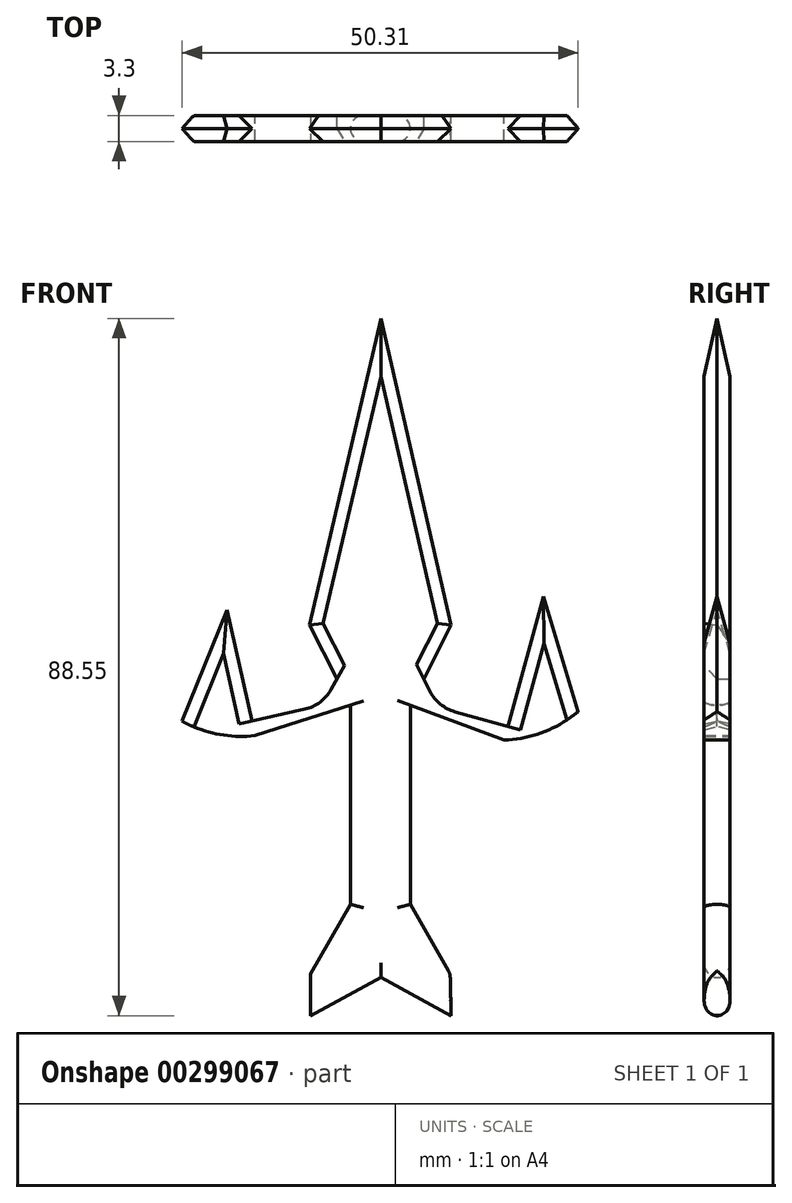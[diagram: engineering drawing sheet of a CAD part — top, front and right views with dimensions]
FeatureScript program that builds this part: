
annotation { "Feature Type Name" : "Feature", "Feature Type Description" : "" }
export const myFeature = defineFeature(function(context is Context, id is Id, definition is map)
    precondition{}
    {
        {
            var Q0;
            Q0=qCreatedBy(makeId("Front.planeOp"),FACE);
            var sketch = newSketch(context, id + "F0", { "sketchPlane" : qUnion([Q0])});
            skLineSegment(sketch, "E0", {"start": v(-8.93, -32.58) * mm, "end": v(0, -27.74) * mm});
            skLineSegment(sketch, "E1", {"start": v(0, -27.74) * mm, "end": v(8.93, -32.58) * mm});
            skLineSegment(sketch, "E2", {"start": v(-8.93, -32.58) * mm, "end": v(-8.93, -27.25) * mm});
            skLineSegment(sketch, "E3", {"start": v(-8.93, -27.25) * mm, "end": v(-3.88, -18.44) * mm});
            skLineSegment(sketch, "E4", {"start": v(-3.88, -18.44) * mm, "end": v(3.74, -18.44) * mm});
            skLineSegment(sketch, "E5", {"start": v(3.74, -18.44) * mm, "end": v(8.8, -27.25) * mm});
            skLineSegment(sketch, "E6", {"start": v(8.8, -27.25) * mm, "end": v(8.93, -32.58) * mm});
            skLineSegment(sketch, "E7", {"start": v(-3.88, -18.44) * mm, "end": v(-3.88, 6.85) * mm});
            skLineSegment(sketch, "E8", {"start": v(3.74, -18.44) * mm, "end": v(3.74, 6.85) * mm});
            skArc(sketch, "E9", {"start": v(-25.25, 4.84) * mm, "mid": v(-20.76, 3.19) * mm, "end": v(-15.98, 3) * mm});
            skArc(sketch, "E10", {"start": v(15.65, 2.42) * mm, "mid": v(20.67, 3.44) * mm, "end": v(25.06, 6.07) * mm});
            skLineSegment(sketch, "E11", {"start": v(-25.25, 4.84) * mm, "end": v(-19.55, 18.97) * mm});
            skLineSegment(sketch, "E12", {"start": v(-19.55, 18.97) * mm, "end": v(-15.98, 3) * mm});
            skLineSegment(sketch, "E13", {"start": v(25.06, 6.07) * mm, "end": v(20.67, 20.66) * mm});
            skPoint(sketch, "E13.endSnap0", {"position": v(20.67, 3.44) * mm});
            skLineSegment(sketch, "E14", {"start": v(20.67, 20.66) * mm, "end": v(15.65, 2.42) * mm});
            skLineSegment(sketch, "E15", {"start": v(-3.88, 6.85) * mm, "end": v(-9.07, 17.03) * mm});
            skLineSegment(sketch, "E16", {"start": v(3.74, 6.85) * mm, "end": v(8.94, 17.03) * mm});
            skLineSegment(sketch, "E17", {"start": v(-9.07, 17.03) * mm, "end": v(0, 55.97) * mm});
            skLineSegment(sketch, "E18", {"start": v(0, 55.97) * mm, "end": v(8.94, 17.03) * mm});
            skLineSegment(sketch, "E19", {"start": v(-5.58, 10.2) * mm, "end": v(-7.45, 6.85) * mm});
            skLineSegment(sketch, "E20", {"start": v(5.45, 10.2) * mm, "end": v(7.27, 6.62) * mm});
            skLineSegment(sketch, "E21", {"start": v(-7.45, 6.85) * mm, "end": v(-16.4, 4.85) * mm});
            skLineSegment(sketch, "E22", {"start": v(7.27, 6.62) * mm, "end": v(16.13, 4.18) * mm});
            skLineSegment(sketch, "E23", {"start": v(-15.98, 3) * mm, "end": v(-3.88, 6.85) * mm});
            skLineSegment(sketch, "E24", {"start": v(3.74, 6.85) * mm, "end": v(15.65, 2.42) * mm});
            skSolve(sketch);
        }
        {
            var Q0;
            Q0 = qSketchRegion(id + "F0", true);
            extrude(context, id + "F1", {"entities" : qUnion([Q0]), "depth" : 3.3 * mm});
        }
        {
            var Q0;
            Q0=makeQuery(id+"F1.opExtrude","CAP_EDGE",EDGE,{"disambiguationData":[OSD([sQuery(id+"F0.wireOp",EDGE,"E18")])],"isStart":false});
            var Q1;
            Q1=makeQuery(id+"F1.opExtrude","CAP_EDGE",EDGE,{"disambiguationData":[OSD([sQuery(id+"F0.wireOp",EDGE,"E17")])],"isStart":false});
            var Q2;
            Q2=makeQuery(id+"F1.opExtrude","CAP_EDGE",EDGE,{"disambiguationData":[OSD([sQuery(id+"F0.wireOp",EDGE,"E14")])],"isStart":false});
            var Q3;
            Q3=makeQuery(id+"F1.opExtrude","CAP_EDGE",EDGE,{"disambiguationData":[OSD([sQuery(id+"F0.wireOp",EDGE,"E13")])],"isStart":false});
            var Q4;
            Q4=makeQuery(id+"F1.opExtrude","CAP_EDGE",EDGE,{"disambiguationData":[OSD([sQuery(id+"F0.wireOp",EDGE,"E11")])],"isStart":false});
            var Q5;
            Q5=makeQuery(id+"F1.opExtrude","CAP_EDGE",EDGE,{"disambiguationData":[OSD([sQuery(id+"F0.wireOp",EDGE,"E12")])],"isStart":false});
            var Q6;
            Q6=makeQuery(id+"F1.opExtrude","CAP_EDGE",EDGE,{"disambiguationData":[OSD([sQuery(id+"F0.wireOp",EDGE,"E14")])],"isStart":true});
            var Q7;
            Q7=makeQuery(id+"F1.opExtrude","CAP_EDGE",EDGE,{"disambiguationData":[OSD([sQuery(id+"F0.wireOp",EDGE,"E13")])],"isStart":true});
            var Q8;
            Q8=makeQuery(id+"F1.opExtrude","CAP_EDGE",EDGE,{"disambiguationData":[OSD([sQuery(id+"F0.wireOp",EDGE,"E11")])],"isStart":true});
            var Q9;
            Q9=makeQuery(id+"F1.opExtrude","CAP_EDGE",EDGE,{"disambiguationData":[OSD([sQuery(id+"F0.wireOp",EDGE,"E12")])],"isStart":true});
            var Q10;
            Q10=makeQuery(id+"F1.opExtrude","CAP_EDGE",EDGE,{"disambiguationData":[OSD([sQuery(id+"F0.wireOp",EDGE,"E16")])],"isStart":false});
            var Q11;
            Q11=makeQuery(id+"F1.opExtrude","CAP_EDGE",EDGE,{"disambiguationData":[OSD([sQuery(id+"F0.wireOp",EDGE,"E15")])],"isStart":false});
            var Q12;
            Q12=makeQuery(id+"F1.opExtrude","CAP_EDGE",EDGE,{"disambiguationData":[OSD([sQuery(id+"F0.wireOp",EDGE,"E18")])],"isStart":true});
            var Q13;
            Q13=makeQuery(id+"F1.opExtrude","CAP_EDGE",EDGE,{"disambiguationData":[OSD([sQuery(id+"F0.wireOp",EDGE,"E17")])],"isStart":true});
            chamfer(context, id + "F2", {"entities" : qUnion([Q0, Q1, Q2, Q3, Q4, Q5, Q6, Q7, Q8, Q9, Q10, Q11, Q12, Q13]), "width" : 1.65 * mm, "tangentPropagation" : true});
        }
        {
            var Q0;
            Q0=makeQuery(id+"F1.opExtrude","SWEPT_EDGE",EDGE,{"disambiguationData":[OSD([sQuery(id+"F0.wireOp",EDGE,"E19"),sQuery(id+"F0.wireOp",EDGE,"E21")])]});
            var Q1;
            Q1=makeQuery(id+"F1.opExtrude","SWEPT_EDGE",EDGE,{"disambiguationData":[OSD([sQuery(id+"F0.wireOp",EDGE,"E20"),sQuery(id+"F0.wireOp",EDGE,"E22")])]});
            fillet(context, id + "F3", {"entities" : qUnion([Q0, Q1]), "radius" : 5.08 * mm, "tangentPropagation" : true, "allowEdgeOverflow" : false});
        }
        {
            var Q0;
            Q0=makeQuery(id+"F1.opExtrude","CAP_EDGE",EDGE,{"disambiguationData":[OSD([sQuery(id+"F0.wireOp",EDGE,"E7")])],"isStart":false});
            var Q1;
            Q1=makeQuery(id+"F1.opExtrude","CAP_EDGE",EDGE,{"disambiguationData":[OSD([sQuery(id+"F0.wireOp",EDGE,"E8")])],"isStart":false});
            var Q2;
            Q2=makeQuery(id+"F1.opExtrude","CAP_EDGE",EDGE,{"disambiguationData":[OSD([sQuery(id+"F0.wireOp",EDGE,"E7")])],"isStart":true});
            var Q3;
            Q3=makeQuery(id+"F1.opExtrude","CAP_EDGE",EDGE,{"disambiguationData":[OSD([sQuery(id+"F0.wireOp",EDGE,"E8")])],"isStart":true});
            var Q4;
            Q4=makeQuery(id+"F1.opExtrude","CAP_EDGE",EDGE,{"disambiguationData":[OSD([sQuery(id+"F0.wireOp",EDGE,"E3")])],"isStart":true});
            var Q5;
            Q5=makeQuery(id+"F1.opExtrude","CAP_EDGE",EDGE,{"disambiguationData":[OSD([sQuery(id+"F0.wireOp",EDGE,"E3")])],"isStart":false});
            var Q6;
            Q6=makeQuery(id+"F1.opExtrude","CAP_EDGE",EDGE,{"disambiguationData":[OSD([sQuery(id+"F0.wireOp",EDGE,"E0")])],"isStart":true});
            var Q7;
            Q7=makeQuery(id+"F1.opExtrude","CAP_EDGE",EDGE,{"disambiguationData":[OSD([sQuery(id+"F0.wireOp",EDGE,"E0")])],"isStart":false});
            var Q8;
            Q8=makeQuery(id+"F1.opExtrude","CAP_EDGE",EDGE,{"disambiguationData":[OSD([sQuery(id+"F0.wireOp",EDGE,"E5")])],"isStart":false});
            var Q9;
            Q9=makeQuery(id+"F1.opExtrude","SWEPT_EDGE",EDGE,{"disambiguationData":[OSD([sQuery(id+"F0.wireOp",EDGE,"E5"),sQuery(id+"F0.wireOp",EDGE,"E6")])]});
            var Q10;
            Q10=makeQuery(id+"F1.opExtrude","CAP_EDGE",EDGE,{"disambiguationData":[OSD([sQuery(id+"F0.wireOp",EDGE,"E5")])],"isStart":true});
            var Q11;
            Q11=makeQuery(id+"F1.opExtrude","CAP_EDGE",EDGE,{"disambiguationData":[OSD([sQuery(id+"F0.wireOp",EDGE,"E1")])],"isStart":true});
            var Q12;
            Q12=makeQuery(id+"F1.opExtrude","CAP_EDGE",EDGE,{"disambiguationData":[OSD([sQuery(id+"F0.wireOp",EDGE,"E1")])],"isStart":false});
            fillet(context, id + "F4", {"entities" : qUnion([Q0, Q1, Q2, Q3, Q4, Q5, Q6, Q7, Q8, Q9, Q10, Q11, Q12]), "radius" : 1.65 * mm, "tangentPropagation" : true, "allowEdgeOverflow" : false});
        }
    });
